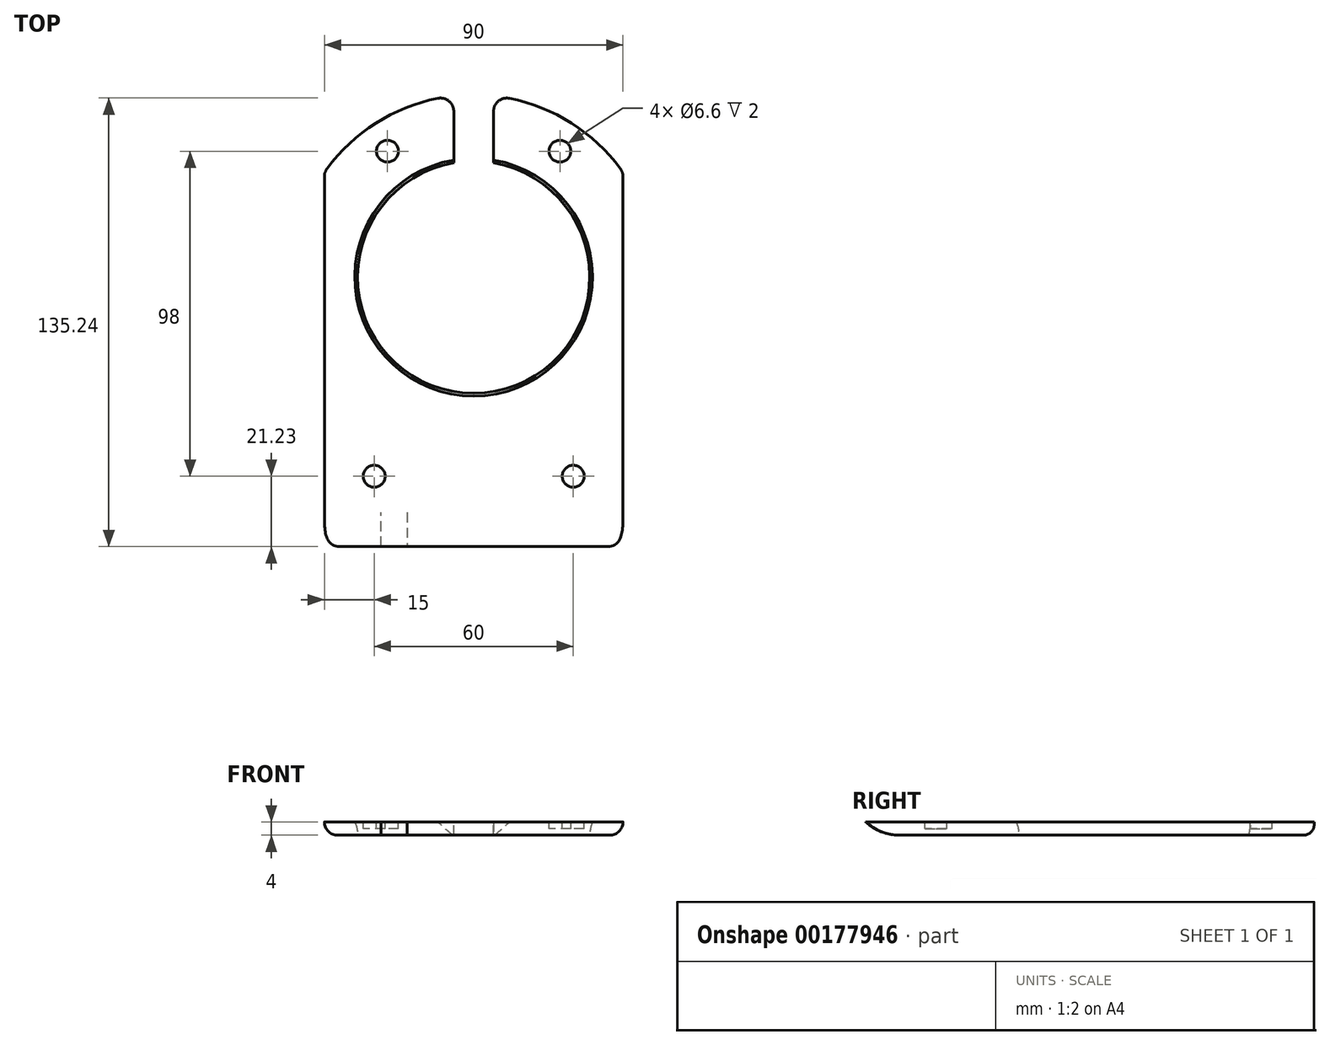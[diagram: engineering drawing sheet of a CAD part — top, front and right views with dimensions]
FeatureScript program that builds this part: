
annotation { "Feature Type Name" : "Feature", "Feature Type Description" : "" }
export const myFeature = defineFeature(function(context is Context, id is Id, definition is map)
    precondition{}
    {
        {
            var Q0;
            Q0=qCreatedBy(makeId("Top.planeOp"),FACE);
            var sketch = newSketch(context, id + "F0", { "sketchPlane" : qUnion([Q0])});
            skCircle(sketch, "E0", {"center": v(0, 0) * mm, "radius": 35 * mm});
            skLineSegment(sketch, "E1.bottom", {"start": v(45, -80) * mm, "end": v(-45, -80) * mm});
            skLineSegment(sketch, "E1.top", {"start": v(45, 80) * mm, "end": v(-45, 80) * mm});
            skLineSegment(sketch, "E1.left", {"start": v(45, -80) * mm, "end": v(45, 80) * mm});
            skLineSegment(sketch, "E1.right", {"start": v(-45, -80) * mm, "end": v(-45, 80) * mm});
            skSolve(sketch);
        }
        {
            var Q0;
            Q0=qSketchRegion(id+"F0",true);
            extrude(context, id + "F1", {"entities" : qUnion([Q0]), "depth" : 10 * mm});
        }
        {
            var Q0;
            Q0=makeQuery(id+"F1.opExtrude","CAP_EDGE",EDGE,{"disambiguationData":[OSD([sQuery(id+"F0.wireOp",EDGE,"E0")])],"isStart":false});
            fillet(context, id + "F2", {"entities" : qUnion([Q0]), "radius" : 10 * mm, "tangentPropagation" : true, "allowEdgeOverflow" : false});
        }
        {
            var Q0;
            Q0=makeQuery(id+"F2.opFillet","SPLIT",FACE,{"disambiguationData":[OD(1.0)],"derivedFrom":makeQuery(id+"F1.opExtrude","CAP_FACE",FACE,{"disambiguationData":[OSD([sQuery(id+"F0.wireOp",EDGE,"E0"),sQuery(id+"F0.wireOp",EDGE,"E1.bottom"),sQuery(id+"F0.wireOp",EDGE,"E1.top"),sQuery(id+"F0.wireOp",EDGE,"E1.left"),sQuery(id+"F0.wireOp",EDGE,"E1.right")])],"isStart":false})});
            var sketch = newSketch(context, id + "F3", { "sketchPlane" : qUnion([Q0])});
            skCircle(sketch, "E2", {"center": v(0, 0) * mm, "radius": 49 * mm});
            skLineSegment(sketch, "E3.bottom", {"start": v(45, -80) * mm, "end": v(-45, -80) * mm});
            skLineSegment(sketch, "E3.top", {"start": v(45, 80) * mm, "end": v(-45, 80) * mm});
            skLineSegment(sketch, "E3.left", {"start": v(45, -80) * mm, "end": v(45, 80) * mm});
            skLineSegment(sketch, "E3.right", {"start": v(-45, -80) * mm, "end": v(-45, 80) * mm});
            skSolve(sketch);
        }
        {
            var Q0;
            {var subQ5=sQuery(id+"F3.wireOp",EDGE,"E3.top");Q0=makeQuery(id+"F3.imprint","IMPRINT",FACE,{"disambiguationData":[TD([[makeQuery(id+"F3.imprint","IMPRINT",EDGE,{"derivedFrom":subQ5}),1.0]])]});}
            var Q1;
            {var subQ5=sQuery(id+"F3.wireOp",EDGE,"E3.bottom");Q1=makeQuery(id+"F3.imprint","IMPRINT",FACE,{"disambiguationData":[TD([[makeQuery(id+"F3.imprint","IMPRINT",EDGE,{"derivedFrom":subQ5}),-1.0]])]});}
            extrude(context, id + "F4", {"entities" : qUnion([Q0, Q1]), "operationType" : NewBodyOperationType.ADD, "depth" : 6 * mm});
        }
        {
            var Q0;
            {var subQ0=sQuery(id+"F3.wireOp",EDGE,"E2");Q0=makeQuery(id+"F4.opExtrude","CAP_EDGE",EDGE,{"disambiguationData":[OSD([subQ0]),TDD([makeQuery(id+"F3.imprint","IMPRINT",EDGE,{"disambiguationData":[TD([[makeQuery(id+"F3.imprint","INTERSECT",VERTEX,{"disambiguationData":[OD(0.0)],"derivedFrom":[subQ0,sQuery(id+"F3.wireOp",EDGE,"E3.right")]}),1.0]])],"derivedFrom":subQ0})])],"isStart":true});}
            var Q1;
            {var subQ0=sQuery(id+"F3.wireOp",EDGE,"E2");Q1=makeQuery(id+"F4.opExtrude","CAP_EDGE",EDGE,{"disambiguationData":[OSD([subQ0]),TDD([makeQuery(id+"F3.imprint","IMPRINT",EDGE,{"disambiguationData":[TD([[makeQuery(id+"F3.imprint","INTERSECT",VERTEX,{"disambiguationData":[OD(0.0)],"derivedFrom":[subQ0,sQuery(id+"F3.wireOp",EDGE,"E3.right")]}),1.0]])],"derivedFrom":subQ0})])],"isStart":false});}
            var Q2;
            {var subQ0=sQuery(id+"F3.wireOp",EDGE,"E2");Q2=makeQuery(id+"F4.opExtrude","CAP_EDGE",EDGE,{"disambiguationData":[OSD([subQ0]),TDD([makeQuery(id+"F3.imprint","IMPRINT",EDGE,{"disambiguationData":[TD([[makeQuery(id+"F3.imprint","INTERSECT",VERTEX,{"disambiguationData":[OD(1.0)],"derivedFrom":[subQ0,sQuery(id+"F3.wireOp",EDGE,"E3.right")]}),-1.0]])],"derivedFrom":subQ0})])],"isStart":true});}
            var Q3;
            {var subQ0=sQuery(id+"F3.wireOp",EDGE,"E2");Q3=makeQuery(id+"F4.opExtrude","CAP_EDGE",EDGE,{"disambiguationData":[OSD([subQ0]),TDD([makeQuery(id+"F3.imprint","IMPRINT",EDGE,{"disambiguationData":[TD([[makeQuery(id+"F3.imprint","INTERSECT",VERTEX,{"disambiguationData":[OD(1.0)],"derivedFrom":[subQ0,sQuery(id+"F3.wireOp",EDGE,"E3.right")]}),-1.0]])],"derivedFrom":subQ0})])],"isStart":false});}
            fillet(context, id + "F5", {"entities" : qUnion([Q0, Q1, Q2, Q3]), "radius" : 2 * mm, "tangentPropagation" : true, "allowEdgeOverflow" : false});
        }
        {
            var Q0;
            Q0=makeQuery(id+"F4.opExtrude","CAP_FACE",FACE,{"disambiguationData":[OSD([sQuery(id+"F3.wireOp",EDGE,"E2"),sQuery(id+"F3.wireOp",EDGE,"E3.top"),sQuery(id+"F3.wireOp",EDGE,"E3.left"),sQuery(id+"F3.wireOp",EDGE,"E3.right")])],"isStart":false});
            var sketch = newSketch(context, id + "F6", { "sketchPlane" : qUnion([Q0])});
            skCircle(sketch, "E4", {"center": v(0, 0) * mm, "radius": 55 * mm});
            skLineSegment(sketch, "E5", {"start": v(-45, 31.62) * mm, "end": v(-45, 80) * mm});
            skLineSegment(sketch, "E6", {"start": v(-45, 80) * mm, "end": v(45, 80) * mm});
            skLineSegment(sketch, "E7", {"start": v(45, 80) * mm, "end": v(45, 31.62) * mm});
            skSolve(sketch);
        }
        {
            var Q0;
            {var subQ0=sQuery(id+"F6.wireOp",EDGE,"E5");Q0=makeQuery(id+"F6.imprint","IMPRINT",FACE,{"disambiguationData":[TD([[makeQuery(id+"F6.imprint","IMPRINT",EDGE,{"derivedFrom":subQ0}),-1.0]])]});}
            extrude(context, id + "F7", {"entities" : qUnion([Q0]), "operationType" : NewBodyOperationType.REMOVE, "endBound" : BoundingType.UP_TO_NEXT, "oppositeDirection" : true, "depth" : 25 * mm});
        }
        {
            var Q0;
            Q0=makeQuery(id+"F4.opExtrude","CAP_FACE",FACE,{"disambiguationData":[OSD([sQuery(id+"F3.wireOp",EDGE,"E2"),sQuery(id+"F3.wireOp",EDGE,"E3.bottom"),sQuery(id+"F3.wireOp",EDGE,"E3.left"),sQuery(id+"F3.wireOp",EDGE,"E3.right")])],"isStart":false});
            var sketch = newSketch(context, id + "F8", { "sketchPlane" : qUnion([Q0])});
            skLineSegment(sketch, "E8.bottom", {"start": v(39, -80) * mm, "end": v(-39, -80) * mm});
            skLineSegment(sketch, "E8.top", {"start": v(39, 80) * mm, "end": v(-39, 80) * mm});
            skLineSegment(sketch, "E8.left", {"start": v(39, -80) * mm, "end": v(39, 80) * mm});
            skLineSegment(sketch, "E8.right", {"start": v(-39, -80) * mm, "end": v(-39, 80) * mm});
            skPoint(sketch, "E8.middle", {"position": v(0, 0) * mm});
            skLineSegment(sketch, "E9.bottom", {"start": v(45, -86) * mm, "end": v(-45, -86) * mm});
            skLineSegment(sketch, "E9.top", {"start": v(45, 86) * mm, "end": v(-45, 86) * mm});
            skLineSegment(sketch, "E9.left", {"start": v(45, -86) * mm, "end": v(45, 86) * mm});
            skLineSegment(sketch, "E9.right", {"start": v(-45, -86) * mm, "end": v(-45, 86) * mm});
            skArc(sketch, "E10", {"start": v(-45, -24) * mm, "mid": v(0, -51) * mm, "end": v(45, -24) * mm});
            skSolve(sketch);
        }
        {
            var Q0;
            {var subQ1=makeQuery(id+"F4.opExtrude","CAP_EDGE",EDGE,{"disambiguationData":[OSD([sQuery(id+"F3.wireOp",EDGE,"E3.bottom")])],"isStart":false});var subQ5=sQuery(id+"F8.wireOp",EDGE,"E9.left");var subQ7=makeQuery(id+"F8.imprint","INTERSECT",VERTEX,{"derivedFrom":[subQ1,subQ5]});Q0=makeQuery(id+"F8.imprint","IMPRINT",FACE,{"disambiguationData":[TD([[makeQuery(id+"F8.imprint","IMPRINT",EDGE,{"disambiguationData":[TD([[subQ7,-1.0]])],"derivedFrom":subQ5}),1.0]])]});}
            var Q1;
            {var subQ1=makeQuery(id+"F4.opExtrude","CAP_EDGE",EDGE,{"disambiguationData":[OSD([sQuery(id+"F3.wireOp",EDGE,"E3.bottom")])],"isStart":false});var subQ5=sQuery(id+"F8.wireOp",EDGE,"E9.right");var subQ6=makeQuery(id+"F8.imprint","INTERSECT",VERTEX,{"derivedFrom":[subQ1,subQ5]});Q1=makeQuery(id+"F8.imprint","IMPRINT",FACE,{"disambiguationData":[TD([[makeQuery(id+"F8.imprint","IMPRINT",EDGE,{"disambiguationData":[TD([[subQ6,-1.0]])],"derivedFrom":subQ5}),-1.0]])]});}
            extrude(context, id + "F9", {"entities" : qUnion([Q0, Q1]), "operationType" : NewBodyOperationType.ADD, "depth" : 7 * mm});
        }
        {
            var Q0;
            Q0=qCreatedBy(makeId("Right.planeOp"),FACE);
            var sketch = newSketch(context, id + "F10", { "sketchPlane" : qUnion([Q0])});
            skLineSegment(sketch, "E11", {"start": v(-64.77, -48.06) * mm, "end": v(-70.53, -49.87) * mm});
            skLineSegment(sketch, "E12", {"start": v(-85.96, 0) * mm, "end": v(-85.96, 23) * mm});
            skLineSegment(sketch, "E13", {"start": v(-79.96, 0) * mm, "end": v(-79.96, 20.33) * mm});
            skLineSegment(sketch, "E14", {"start": v(-79.96, 0) * mm, "end": v(-85.96, 0) * mm});
            skLineSegment(sketch, "E15", {"start": v(-85.96, 23) * mm, "end": v(-77.63, 23) * mm});
            skLineSegment(sketch, "E16", {"start": v(-77.63, 23) * mm, "end": v(-79.96, 20.33) * mm});
            skSolve(sketch);
        }
        {
            var Q0;
            Q0=qSketchRegion(id+"F10",true);
            extrude(context, id + "F11", {"entities" : qUnion([Q0]), "operationType" : NewBodyOperationType.ADD, "depth" : 45 * mm, "hasSecondDirection" : true, "secondDirectionOppositeDirection" : true, "secondDirectionDepth" : 45 * mm});
        }
        {
            var Q0;
            Q0=makeQuery(id+"F11.opExtrude","SWEPT_FACE",FACE,{"disambiguationData":[OSD([sQuery(id+"F10.wireOp",EDGE,"E12")])]});
            var sketch = newSketch(context, id + "F12", { "sketchPlane" : qUnion([Q0])});
            skCircle(sketch, "E17", {"center": v(-24, 19.53) * mm, "radius": 4 * mm});
            skSolve(sketch);
        }
        {
            var Q0;
            Q0=qSketchRegion(id+"F12",true);
            extrude(context, id + "F13", {"entities" : qUnion([Q0]), "operationType" : NewBodyOperationType.REMOVE, "oppositeDirection" : true, "depth" : 8.5 * mm});
        }
        {
            var Q0;
            Q0=qCreatedBy(makeId("Front.planeOp"),FACE);
            var sketch = newSketch(context, id + "F14", { "sketchPlane" : qUnion([Q0])});
            skLineSegment(sketch, "E18.bottom", {"start": v(-6, 0) * mm, "end": v(6, 0) * mm});
            skLineSegment(sketch, "E18.top", {"start": v(-6, 12) * mm, "end": v(6, 12) * mm});
            skLineSegment(sketch, "E18.left", {"start": v(-6, 0) * mm, "end": v(-6, 12) * mm});
            skLineSegment(sketch, "E18.right", {"start": v(6, 0) * mm, "end": v(6, 12) * mm});
            skPoint(sketch, "E18.middle", {"position": v(0, 6) * mm});
            skSolve(sketch);
        }
        {
            var Q0;
            Q0=qSketchRegion(id+"F14",true);
            extrude(context, id + "F15", {"entities" : qUnion([Q0]), "operationType" : NewBodyOperationType.REMOVE, "endBound" : BoundingType.THROUGH_ALL, "oppositeDirection" : true, "depth" : 25 * mm});
        }
        {
            var Q0;
            Q0=makeQuery(id+"F7.boolean.opBoolean","COPY",FACE,{"derivedFrom":makeQuery(id+"F7.opExtrude","SWEPT_FACE",FACE,{"disambiguationData":[OSD([sQuery(id+"F6.wireOp",EDGE,"E4")])]})});
            var Q1;
            Q1=makeQuery(id+"F15.boolean.opBoolean","COPY",EDGE,{"derivedFrom":makeQuery(id+"F15.opExtrude","SWEPT_EDGE",EDGE,{"disambiguationData":[OSD([sQuery(id+"F14.wireOp",EDGE,"E18.bottom"),sQuery(id+"F14.wireOp",EDGE,"E18.left")])]})});
            var Q2;
            Q2=makeQuery(id+"F15.boolean.opBoolean","COPY",EDGE,{"derivedFrom":makeQuery(id+"F15.opExtrude","SWEPT_EDGE",EDGE,{"disambiguationData":[OSD([sQuery(id+"F14.wireOp",EDGE,"E18.bottom"),sQuery(id+"F14.wireOp",EDGE,"E18.right")])]})});
            var Q3;
            Q3=makeQuery(id+"F11.boolean.opBoolean","MERGE",EDGE,{"derivedFrom":[makeQuery(id+"F1.opExtrude","CAP_EDGE",EDGE,{"disambiguationData":[OSD([sQuery(id+"F0.wireOp",EDGE,"E1.left")])],"isStart":true}),makeQuery(id+"F11.opExtrude","CAP_EDGE",EDGE,{"disambiguationData":[OSD([sQuery(id+"F10.wireOp",EDGE,"E14")])],"isStart":false})]});
            var Q4;
            Q4=makeQuery(id+"F11.boolean.opBoolean","MERGE",EDGE,{"derivedFrom":[makeQuery(id+"F1.opExtrude","CAP_EDGE",EDGE,{"disambiguationData":[OSD([sQuery(id+"F0.wireOp",EDGE,"E1.right")])],"isStart":true}),makeQuery(id+"F11.opExtrude","CAP_EDGE",EDGE,{"disambiguationData":[OSD([sQuery(id+"F10.wireOp",EDGE,"E14")])],"isStart":true})]});
            var Q5;
            Q5=makeQuery(id+"F11.opExtrude","CAP_EDGE",EDGE,{"disambiguationData":[OSD([sQuery(id+"F10.wireOp",EDGE,"E12")])],"isStart":false});
            var Q6;
            Q6=makeQuery(id+"F11.opExtrude","CAP_EDGE",EDGE,{"disambiguationData":[OSD([sQuery(id+"F10.wireOp",EDGE,"E12")])],"isStart":true});
            var Q7;
            Q7=makeQuery(id+"F11.boolean.opBoolean","MERGE",EDGE,{"derivedFrom":[makeQuery(id+"F9.opExtrude","CAP_EDGE",EDGE,{"disambiguationData":[OSD([sQuery(id+"F8.wireOp",EDGE,"E9.right")])],"isStart":false}),makeQuery(id+"F11.opExtrude","CAP_EDGE",EDGE,{"disambiguationData":[OSD([sQuery(id+"F10.wireOp",EDGE,"E15")])],"isStart":true})]});
            var Q8;
            Q8=makeQuery(id+"F11.boolean.opBoolean","MERGE",EDGE,{"derivedFrom":[makeQuery(id+"F9.opExtrude","CAP_EDGE",EDGE,{"disambiguationData":[OSD([sQuery(id+"F8.wireOp",EDGE,"E9.left")])],"isStart":false}),makeQuery(id+"F11.opExtrude","CAP_EDGE",EDGE,{"disambiguationData":[OSD([sQuery(id+"F10.wireOp",EDGE,"E15")])],"isStart":false})]});
            var Q9;
            {var subQ5=sQuery(id+"F10.wireOp",EDGE,"E12");var subQ6=sQuery(id+"F10.wireOp",EDGE,"E15");Q9=makeQuery(id+"F13.boolean.opBoolean","SPLIT",EDGE,{"disambiguationData":[TD([makeQuery(id+"F1.opExtrude","SWEPT_FACE",FACE,{"disambiguationData":[OSD([sQuery(id+"F0.wireOp",EDGE,"E1.left")])]})])],"derivedFrom":makeQuery(id+"F11.opExtrude","SWEPT_EDGE",EDGE,{"disambiguationData":[OSD([subQ5,subQ6])]})});}
            var Q10;
            {var subQ5=sQuery(id+"F10.wireOp",EDGE,"E15");var subQ6=sQuery(id+"F10.wireOp",EDGE,"E12");Q10=makeQuery(id+"F13.boolean.opBoolean","SPLIT",EDGE,{"disambiguationData":[TD([makeQuery(id+"F1.opExtrude","SWEPT_FACE",FACE,{"disambiguationData":[OSD([sQuery(id+"F0.wireOp",EDGE,"E1.right")])]})])],"derivedFrom":makeQuery(id+"F11.opExtrude","SWEPT_EDGE",EDGE,{"disambiguationData":[OSD([subQ6,subQ5])]})});}
            var Q11;
            Q11=makeQuery(id+"F13.boolean.opBoolean","COPY",EDGE,{"derivedFrom":makeQuery(id+"F13.opExtrude","CAP_EDGE",EDGE,{"disambiguationData":[OSD([sQuery(id+"F12.wireOp",EDGE,"E17")])],"isStart":true})});
            fillet(context, id + "F16", {"entities" : qUnion([Q0, Q1, Q2, Q3, Q4, Q5, Q6, Q7, Q8, Q9, Q10, Q11]), "radius" : 4 * mm, "tangentPropagation" : true, "allowEdgeOverflow" : false});
        }
        {
            var Q0;
            {var subQ0=sQuery(id+"F8.wireOp",EDGE,"E10");var subQ1=sQuery(id+"F3.wireOp",EDGE,"E3.bottom");Q0=makeQuery(id+"F13.boolean.opBoolean","INTERSECT",EDGE,{"disambiguationData":[OD(1.0)],"derivedFrom":[makeQuery(id+"F11.boolean.opBoolean","MERGE",FACE,{"derivedFrom":[makeQuery(id+"F9.opExtrude","CAP_FACE",FACE,{"disambiguationData":[OSD([subQ1,sQuery(id+"F8.wireOp",EDGE,"E8.left"),sQuery(id+"F8.wireOp",EDGE,"E9.left"),subQ0])],"isStart":false}),makeQuery(id+"F9.opExtrude","CAP_FACE",FACE,{"disambiguationData":[OSD([subQ1,sQuery(id+"F8.wireOp",EDGE,"E8.right"),sQuery(id+"F8.wireOp",EDGE,"E9.right"),subQ0])],"isStart":false}),makeQuery(id+"F11.opExtrude","SWEPT_FACE",FACE,{"disambiguationData":[OSD([sQuery(id+"F10.wireOp",EDGE,"E15")])]})]}),makeQuery(id+"F13.opExtrude","SWEPT_FACE",FACE,{"disambiguationData":[OSD([sQuery(id+"F12.wireOp",EDGE,"E17")])]})]});}
            var Q1;
            {var subQ0=sQuery(id+"F8.wireOp",EDGE,"E10");var subQ1=sQuery(id+"F3.wireOp",EDGE,"E3.bottom");Q1=makeQuery(id+"F13.boolean.opBoolean","INTERSECT",EDGE,{"disambiguationData":[OD(0.0)],"derivedFrom":[makeQuery(id+"F11.boolean.opBoolean","MERGE",FACE,{"derivedFrom":[makeQuery(id+"F9.opExtrude","CAP_FACE",FACE,{"disambiguationData":[OSD([subQ1,sQuery(id+"F8.wireOp",EDGE,"E8.left"),sQuery(id+"F8.wireOp",EDGE,"E9.left"),subQ0])],"isStart":false}),makeQuery(id+"F9.opExtrude","CAP_FACE",FACE,{"disambiguationData":[OSD([subQ1,sQuery(id+"F8.wireOp",EDGE,"E8.right"),sQuery(id+"F8.wireOp",EDGE,"E9.right"),subQ0])],"isStart":false}),makeQuery(id+"F11.opExtrude","SWEPT_FACE",FACE,{"disambiguationData":[OSD([sQuery(id+"F10.wireOp",EDGE,"E15")])]})]}),makeQuery(id+"F13.opExtrude","SWEPT_FACE",FACE,{"disambiguationData":[OSD([sQuery(id+"F12.wireOp",EDGE,"E17")])]})]});}
            var Q2;
            Q2=makeQuery(id+"F13.boolean.opBoolean","COPY",EDGE,{"derivedFrom":makeQuery(id+"F13.opExtrude","CAP_EDGE",EDGE,{"disambiguationData":[OSD([sQuery(id+"F12.wireOp",EDGE,"E17")])],"isStart":false})});
            var Q3;
            Q3=makeQuery(id+"F9.opExtrude","CAP_EDGE",EDGE,{"disambiguationData":[OSD([sQuery(id+"F8.wireOp",EDGE,"E8.left")])],"isStart":true});
            var Q4;
            Q4=makeQuery(id+"F9.opExtrude","CAP_EDGE",EDGE,{"disambiguationData":[OSD([sQuery(id+"F8.wireOp",EDGE,"E8.right")])],"isStart":true});
            var Q5;
            Q5=makeQuery(id+"F9.opExtrude","CAP_EDGE",EDGE,{"disambiguationData":[OSD([sQuery(id+"F8.wireOp",EDGE,"E8.right")])],"isStart":false});
            var Q6;
            Q6=makeQuery(id+"F9.opExtrude","CAP_EDGE",EDGE,{"disambiguationData":[OSD([sQuery(id+"F8.wireOp",EDGE,"E8.left")])],"isStart":false});
            var Q7;
            {var subQ0=sQuery(id+"F3.wireOp",EDGE,"E3.left");var subQ1=sQuery(id+"F3.wireOp",EDGE,"E2");Q7=makeQuery(id+"F5.opFillet","BLEND_EDGE",EDGE,{"blendedFrom":[makeQuery(id+"F4.opExtrude","CAP_EDGE",EDGE,{"disambiguationData":[OSD([subQ1]),TDD([makeQuery(id+"F3.imprint","IMPRINT",EDGE,{"disambiguationData":[TD([[makeQuery(id+"F3.imprint","INTERSECT",VERTEX,{"disambiguationData":[OD(1.0)],"derivedFrom":[subQ1,sQuery(id+"F3.wireOp",EDGE,"E3.right")]}),-1.0]])],"derivedFrom":subQ1})])],"isStart":false}),makeQuery(id+"F4.boolean.opBoolean","MERGE",FACE,{"derivedFrom":[makeQuery(id+"F1.opExtrude","SWEPT_FACE",FACE,{"disambiguationData":[OSD([sQuery(id+"F0.wireOp",EDGE,"E1.left")])]}),makeQuery(id+"F4.opExtrude","SWEPT_FACE",FACE,{"disambiguationData":[OSD([subQ0]),TDD([makeQuery(id+"F3.imprint","IMPRINT",EDGE,{"disambiguationData":[TD([[makeQuery(id+"F3.imprint","INTERSECT",VERTEX,{"derivedFrom":[sQuery(id+"F3.wireOp",EDGE,"E3.bottom"),subQ0]}),-1.0]])],"derivedFrom":subQ0})])]}),makeQuery(id+"F4.opExtrude","SWEPT_FACE",FACE,{"disambiguationData":[OSD([subQ0]),TDD([makeQuery(id+"F3.imprint","IMPRINT",EDGE,{"disambiguationData":[TD([[makeQuery(id+"F3.imprint","INTERSECT",VERTEX,{"derivedFrom":[sQuery(id+"F3.wireOp",EDGE,"E3.top"),subQ0]}),1.0]])],"derivedFrom":subQ0})])]})]})],"blendedInto":[makeQuery(id+"F4.boolean.opBoolean","MERGE",FACE,{"derivedFrom":[makeQuery(id+"F1.opExtrude","SWEPT_FACE",FACE,{"disambiguationData":[OSD([sQuery(id+"F0.wireOp",EDGE,"E1.left")])]}),makeQuery(id+"F4.opExtrude","SWEPT_FACE",FACE,{"disambiguationData":[OSD([subQ0]),TDD([makeQuery(id+"F3.imprint","IMPRINT",EDGE,{"disambiguationData":[TD([[makeQuery(id+"F3.imprint","INTERSECT",VERTEX,{"derivedFrom":[sQuery(id+"F3.wireOp",EDGE,"E3.bottom"),subQ0]}),-1.0]])],"derivedFrom":subQ0})])]}),makeQuery(id+"F4.opExtrude","SWEPT_FACE",FACE,{"disambiguationData":[OSD([subQ0]),TDD([makeQuery(id+"F3.imprint","IMPRINT",EDGE,{"disambiguationData":[TD([[makeQuery(id+"F3.imprint","INTERSECT",VERTEX,{"derivedFrom":[sQuery(id+"F3.wireOp",EDGE,"E3.top"),subQ0]}),1.0]])],"derivedFrom":subQ0})])]})]})]});}
            var Q8;
            {var subQ0=sQuery(id+"F3.wireOp",EDGE,"E3.right");var subQ1=sQuery(id+"F3.wireOp",EDGE,"E2");var subQ2=makeQuery(id+"F3.imprint","INTERSECT",VERTEX,{"disambiguationData":[OD(1.0)],"derivedFrom":[subQ1,subQ0]});Q8=makeQuery(id+"F5.opFillet","BLEND_EDGE",EDGE,{"blendedFrom":[makeQuery(id+"F4.opExtrude","CAP_EDGE",EDGE,{"disambiguationData":[OSD([subQ1]),TDD([makeQuery(id+"F3.imprint","IMPRINT",EDGE,{"disambiguationData":[TD([[subQ2,-1.0]])],"derivedFrom":subQ1})])],"isStart":false}),makeQuery(id+"F4.boolean.opBoolean","MERGE",FACE,{"derivedFrom":[makeQuery(id+"F1.opExtrude","SWEPT_FACE",FACE,{"disambiguationData":[OSD([sQuery(id+"F0.wireOp",EDGE,"E1.right")])]}),makeQuery(id+"F4.opExtrude","SWEPT_FACE",FACE,{"disambiguationData":[OSD([subQ0]),TDD([makeQuery(id+"F3.imprint","IMPRINT",EDGE,{"disambiguationData":[TD([[makeQuery(id+"F3.imprint","INTERSECT",VERTEX,{"derivedFrom":[sQuery(id+"F3.wireOp",EDGE,"E3.bottom"),subQ0]}),-1.0]])],"derivedFrom":subQ0})])]}),makeQuery(id+"F4.opExtrude","SWEPT_FACE",FACE,{"disambiguationData":[OSD([subQ0]),TDD([makeQuery(id+"F3.imprint","IMPRINT",EDGE,{"disambiguationData":[TD([[makeQuery(id+"F3.imprint","INTERSECT",VERTEX,{"derivedFrom":[sQuery(id+"F3.wireOp",EDGE,"E3.top"),subQ0]}),1.0]])],"derivedFrom":subQ0})])]})]})],"blendedInto":[makeQuery(id+"F4.boolean.opBoolean","MERGE",FACE,{"derivedFrom":[makeQuery(id+"F1.opExtrude","SWEPT_FACE",FACE,{"disambiguationData":[OSD([sQuery(id+"F0.wireOp",EDGE,"E1.right")])]}),makeQuery(id+"F4.opExtrude","SWEPT_FACE",FACE,{"disambiguationData":[OSD([subQ0]),TDD([makeQuery(id+"F3.imprint","IMPRINT",EDGE,{"disambiguationData":[TD([[makeQuery(id+"F3.imprint","INTERSECT",VERTEX,{"derivedFrom":[sQuery(id+"F3.wireOp",EDGE,"E3.bottom"),subQ0]}),-1.0]])],"derivedFrom":subQ0})])]}),makeQuery(id+"F4.opExtrude","SWEPT_FACE",FACE,{"disambiguationData":[OSD([subQ0]),TDD([makeQuery(id+"F3.imprint","IMPRINT",EDGE,{"disambiguationData":[TD([[makeQuery(id+"F3.imprint","INTERSECT",VERTEX,{"derivedFrom":[sQuery(id+"F3.wireOp",EDGE,"E3.top"),subQ0]}),1.0]])],"derivedFrom":subQ0})])]})]})]});}
            fillet(context, id + "F17", {"entities" : qUnion([Q0, Q1, Q2, Q3, Q4, Q5, Q6, Q7, Q8]), "radius" : 2 * mm, "tangentPropagation" : true, "allowEdgeOverflow" : false});
        }
        {
            var Q0;
            {var subQ0=sQuery(id+"F8.wireOp",EDGE,"E10");var subQ1=sQuery(id+"F3.wireOp",EDGE,"E3.left");var subQ2=sQuery(id+"F3.wireOp",EDGE,"E2");Q0=makeQuery(id+"F17.opFillet","BLEND_EDGE",EDGE,{"blendedFrom":[makeQuery(id+"F4.opExtrude","SWEPT_EDGE",EDGE,{"disambiguationData":[OSD([subQ2,subQ1]),TDD([makeQuery(id+"F3.imprint","INTERSECT",VERTEX,{"disambiguationData":[OD(1.0)],"derivedFrom":[subQ2,subQ1]})])]}),makeQuery(id+"F9.opExtrude","SWEPT_FACE",FACE,{"disambiguationData":[OSD([subQ0]),TDD([makeQuery(id+"F8.imprint","IMPRINT",EDGE,{"disambiguationData":[TD([[makeQuery(id+"F8.imprint","INTERSECT",VERTEX,{"derivedFrom":[sQuery(id+"F8.wireOp",EDGE,"E9.left"),subQ0]}),-1.0]])],"derivedFrom":subQ0})])]})],"blendedInto":[makeQuery(id+"F9.opExtrude","SWEPT_FACE",FACE,{"disambiguationData":[OSD([subQ0]),TDD([makeQuery(id+"F8.imprint","IMPRINT",EDGE,{"disambiguationData":[TD([[makeQuery(id+"F8.imprint","INTERSECT",VERTEX,{"derivedFrom":[sQuery(id+"F8.wireOp",EDGE,"E9.left"),subQ0]}),-1.0]])],"derivedFrom":subQ0})])]})]});}
            var Q1;
            {var subQ0=sQuery(id+"F8.wireOp",EDGE,"E10");var subQ1=sQuery(id+"F3.wireOp",EDGE,"E3.right");var subQ2=sQuery(id+"F3.wireOp",EDGE,"E2");Q1=makeQuery(id+"F17.opFillet","BLEND_EDGE",EDGE,{"blendedFrom":[makeQuery(id+"F4.opExtrude","SWEPT_EDGE",EDGE,{"disambiguationData":[OSD([subQ2,subQ1]),TDD([makeQuery(id+"F3.imprint","INTERSECT",VERTEX,{"disambiguationData":[OD(1.0)],"derivedFrom":[subQ2,subQ1]})])]}),makeQuery(id+"F9.opExtrude","SWEPT_FACE",FACE,{"disambiguationData":[OSD([subQ0]),TDD([makeQuery(id+"F8.imprint","IMPRINT",EDGE,{"disambiguationData":[TD([[makeQuery(id+"F8.imprint","INTERSECT",VERTEX,{"derivedFrom":[sQuery(id+"F8.wireOp",EDGE,"E9.right"),subQ0]}),1.0]])],"derivedFrom":subQ0})])]})],"blendedInto":[makeQuery(id+"F9.opExtrude","SWEPT_FACE",FACE,{"disambiguationData":[OSD([subQ0]),TDD([makeQuery(id+"F8.imprint","IMPRINT",EDGE,{"disambiguationData":[TD([[makeQuery(id+"F8.imprint","INTERSECT",VERTEX,{"derivedFrom":[sQuery(id+"F8.wireOp",EDGE,"E9.right"),subQ0]}),1.0]])],"derivedFrom":subQ0})])]})]});}
            var Q2;
            {var subQ0=sQuery(id+"F3.wireOp",EDGE,"E3.right");var subQ1=sQuery(id+"F3.wireOp",EDGE,"E2");var subQ2=makeQuery(id+"F3.imprint","INTERSECT",VERTEX,{"disambiguationData":[OD(1.0)],"derivedFrom":[subQ1,subQ0]});Q2=makeQuery(id+"F17.opFillet","BLEND_EDGE",EDGE,{"blendedFrom":[makeQuery(id+"F4.opExtrude","SWEPT_EDGE",EDGE,{"disambiguationData":[OSD([subQ1,subQ0]),TDD([subQ2])]}),makeQuery(id+"F5.opFillet","BLEND_FACE",FACE,{"disambiguationData":[OSD([subQ1]),TDD([makeQuery(id+"F4.opExtrude","CAP_EDGE",EDGE,{"disambiguationData":[OSD([subQ1]),TDD([makeQuery(id+"F3.imprint","IMPRINT",EDGE,{"disambiguationData":[TD([[subQ2,-1.0]])],"derivedFrom":subQ1})])],"isStart":false})])]})],"blendedInto":[makeQuery(id+"F5.opFillet","BLEND_FACE",FACE,{"disambiguationData":[OSD([subQ1]),TDD([makeQuery(id+"F4.opExtrude","CAP_EDGE",EDGE,{"disambiguationData":[OSD([subQ1]),TDD([makeQuery(id+"F3.imprint","IMPRINT",EDGE,{"disambiguationData":[TD([[subQ2,-1.0]])],"derivedFrom":subQ1})])],"isStart":false})])]})]});}
            var Q3;
            {var subQ0=sQuery(id+"F3.wireOp",EDGE,"E2");var subQ1=sQuery(id+"F3.wireOp",EDGE,"E3.left");var subQ2=makeQuery(id+"F3.imprint","INTERSECT",VERTEX,{"disambiguationData":[OD(1.0)],"derivedFrom":[subQ0,subQ1]});Q3=makeQuery(id+"F17.opFillet","BLEND_EDGE",EDGE,{"blendedFrom":[makeQuery(id+"F4.opExtrude","SWEPT_EDGE",EDGE,{"disambiguationData":[OSD([subQ0,subQ1]),TDD([subQ2])]}),makeQuery(id+"F5.opFillet","BLEND_FACE",FACE,{"disambiguationData":[OSD([subQ0]),TDD([makeQuery(id+"F4.opExtrude","CAP_EDGE",EDGE,{"disambiguationData":[OSD([subQ0]),TDD([makeQuery(id+"F3.imprint","IMPRINT",EDGE,{"disambiguationData":[TD([[makeQuery(id+"F3.imprint","INTERSECT",VERTEX,{"disambiguationData":[OD(1.0)],"derivedFrom":[subQ0,sQuery(id+"F3.wireOp",EDGE,"E3.right")]}),-1.0]])],"derivedFrom":subQ0})])],"isStart":false})])]})],"blendedInto":[makeQuery(id+"F5.opFillet","BLEND_FACE",FACE,{"disambiguationData":[OSD([subQ0]),TDD([makeQuery(id+"F4.opExtrude","CAP_EDGE",EDGE,{"disambiguationData":[OSD([subQ0]),TDD([makeQuery(id+"F3.imprint","IMPRINT",EDGE,{"disambiguationData":[TD([[makeQuery(id+"F3.imprint","INTERSECT",VERTEX,{"disambiguationData":[OD(1.0)],"derivedFrom":[subQ0,sQuery(id+"F3.wireOp",EDGE,"E3.right")]}),-1.0]])],"derivedFrom":subQ0})])],"isStart":false})])]})]});}
            var Q4;
            {var subQ0=sQuery(id+"F8.wireOp",EDGE,"E10");var subQ1=sQuery(id+"F8.wireOp",EDGE,"E9.right");Q4=makeQuery(id+"F16.opFillet","BLEND_EDGE",EDGE,{"blendedFrom":[makeQuery(id+"F11.boolean.opBoolean","MERGE",EDGE,{"derivedFrom":[makeQuery(id+"F9.opExtrude","CAP_EDGE",EDGE,{"disambiguationData":[OSD([subQ1])],"isStart":false}),makeQuery(id+"F11.opExtrude","CAP_EDGE",EDGE,{"disambiguationData":[OSD([sQuery(id+"F10.wireOp",EDGE,"E15")])],"isStart":true})]}),makeQuery(id+"F9.opExtrude","SWEPT_FACE",FACE,{"disambiguationData":[OSD([subQ0]),TDD([makeQuery(id+"F8.imprint","IMPRINT",EDGE,{"disambiguationData":[TD([[makeQuery(id+"F8.imprint","INTERSECT",VERTEX,{"derivedFrom":[subQ1,subQ0]}),1.0]])],"derivedFrom":subQ0})])]})],"blendedInto":[makeQuery(id+"F9.opExtrude","SWEPT_FACE",FACE,{"disambiguationData":[OSD([subQ0]),TDD([makeQuery(id+"F8.imprint","IMPRINT",EDGE,{"disambiguationData":[TD([[makeQuery(id+"F8.imprint","INTERSECT",VERTEX,{"derivedFrom":[subQ1,subQ0]}),1.0]])],"derivedFrom":subQ0})])]})]});}
            var Q5;
            {var subQ0=sQuery(id+"F8.wireOp",EDGE,"E10");var subQ1=sQuery(id+"F8.wireOp",EDGE,"E9.left");Q5=makeQuery(id+"F16.opFillet","BLEND_EDGE",EDGE,{"blendedFrom":[makeQuery(id+"F11.boolean.opBoolean","MERGE",EDGE,{"derivedFrom":[makeQuery(id+"F9.opExtrude","CAP_EDGE",EDGE,{"disambiguationData":[OSD([subQ1])],"isStart":false}),makeQuery(id+"F11.opExtrude","CAP_EDGE",EDGE,{"disambiguationData":[OSD([sQuery(id+"F10.wireOp",EDGE,"E15")])],"isStart":false})]}),makeQuery(id+"F9.opExtrude","SWEPT_FACE",FACE,{"disambiguationData":[OSD([subQ0]),TDD([makeQuery(id+"F8.imprint","IMPRINT",EDGE,{"disambiguationData":[TD([[makeQuery(id+"F8.imprint","INTERSECT",VERTEX,{"derivedFrom":[subQ1,subQ0]}),-1.0]])],"derivedFrom":subQ0})])]})],"blendedInto":[makeQuery(id+"F9.opExtrude","SWEPT_FACE",FACE,{"disambiguationData":[OSD([subQ0]),TDD([makeQuery(id+"F8.imprint","IMPRINT",EDGE,{"disambiguationData":[TD([[makeQuery(id+"F8.imprint","INTERSECT",VERTEX,{"derivedFrom":[subQ1,subQ0]}),-1.0]])],"derivedFrom":subQ0})])]})]});}
            var Q6;
            {var subQ0=sQuery(id+"F10.wireOp",EDGE,"E15");var subQ3=sQuery(id+"F8.wireOp",EDGE,"E8.left");var subQ4=sQuery(id+"F10.wireOp",EDGE,"E16");Q6=makeQuery(id+"F13.boolean.opBoolean","SPLIT",EDGE,{"disambiguationData":[TD([makeQuery(id+"F9.opExtrude","SWEPT_FACE",FACE,{"disambiguationData":[OSD([subQ3])]})])],"derivedFrom":makeQuery(id+"F11.opExtrude","SWEPT_EDGE",EDGE,{"disambiguationData":[OSD([subQ0,subQ4])]})});}
            var Q7;
            {var subQ0=sQuery(id+"F10.wireOp",EDGE,"E15");var subQ2=sQuery(id+"F8.wireOp",EDGE,"E8.right");var subQ4=sQuery(id+"F10.wireOp",EDGE,"E16");Q7=makeQuery(id+"F13.boolean.opBoolean","SPLIT",EDGE,{"disambiguationData":[TD([makeQuery(id+"F9.opExtrude","SWEPT_FACE",FACE,{"disambiguationData":[OSD([subQ2])]})])],"derivedFrom":makeQuery(id+"F11.opExtrude","SWEPT_EDGE",EDGE,{"disambiguationData":[OSD([subQ0,subQ4])]})});}
            var Q8;
            Q8=makeQuery(id+"F15.boolean.opBoolean","COPY",EDGE,{"derivedFrom":makeQuery(id+"F15.opExtrude","SWEPT_EDGE",EDGE,{"disambiguationData":[OSD([sQuery(id+"F14.wireOp",EDGE,"E18.top"),sQuery(id+"F14.wireOp",EDGE,"E18.right")])]})});
            var Q9;
            Q9=makeQuery(id+"F15.boolean.opBoolean","COPY",EDGE,{"derivedFrom":makeQuery(id+"F15.opExtrude","SWEPT_EDGE",EDGE,{"disambiguationData":[OSD([sQuery(id+"F14.wireOp",EDGE,"E18.top"),sQuery(id+"F14.wireOp",EDGE,"E18.left")])]})});
            fillet(context, id + "F18", {"entities" : qUnion([Q0, Q1, Q2, Q3, Q4, Q5, Q6, Q7, Q8, Q9]), "radius" : 1 * mm, "tangentPropagation" : true, "allowEdgeOverflow" : false});
        }
        {
            var Q0;
            Q0=makeQuery(id+"F11.opExtrude","SWEPT_EDGE",EDGE,{"disambiguationData":[OSD([sQuery(id+"F10.wireOp",EDGE,"E12"),sQuery(id+"F10.wireOp",EDGE,"E14")])]});
            fillet(context, id + "F19", {"entities" : qUnion([Q0]), "radius" : 15 * mm, "tangentPropagation" : true, "allowEdgeOverflow" : false});
        }
        {
            var Q0;
            {var subQ0=sQuery(id+"F8.wireOp",EDGE,"E8.left");var subQ3=sQuery(id+"F8.wireOp",EDGE,"E9.left");var subQ4=sQuery(id+"F3.wireOp",EDGE,"E3.bottom");var subQ5=sQuery(id+"F8.wireOp",EDGE,"E10");var subQ8=sQuery(id+"F10.wireOp",EDGE,"E15");Q0=makeQuery(id+"F13.boolean.opBoolean","SPLIT",FACE,{"disambiguationData":[TD([makeQuery(id+"F1.opExtrude","SWEPT_FACE",FACE,{"disambiguationData":[OSD([sQuery(id+"F0.wireOp",EDGE,"E1.left")])]})])],"derivedFrom":makeQuery(id+"F11.boolean.opBoolean","MERGE",FACE,{"derivedFrom":[makeQuery(id+"F9.opExtrude","CAP_FACE",FACE,{"disambiguationData":[OSD([subQ4,subQ0,subQ3,subQ5])],"isStart":false}),makeQuery(id+"F9.opExtrude","CAP_FACE",FACE,{"disambiguationData":[OSD([subQ4,sQuery(id+"F8.wireOp",EDGE,"E8.right"),sQuery(id+"F8.wireOp",EDGE,"E9.right"),subQ5])],"isStart":false}),makeQuery(id+"F11.opExtrude","SWEPT_FACE",FACE,{"disambiguationData":[OSD([subQ8])]})]})});}
            var sketch = newSketch(context, id + "F20", { "sketchPlane" : qUnion([Q0])});
            skLineSegment(sketch, "E19.bottom", {"start": v(47.13, -87.88) * mm, "end": v(-47.13, -87.88) * mm});
            skLineSegment(sketch, "E19.top", {"start": v(47.13, 87.88) * mm, "end": v(-47.13, 87.88) * mm});
            skLineSegment(sketch, "E19.left", {"start": v(47.13, -87.88) * mm, "end": v(47.13, 87.88) * mm});
            skLineSegment(sketch, "E19.right", {"start": v(-47.13, -87.88) * mm, "end": v(-47.13, 87.88) * mm});
            skPoint(sketch, "E19.middle", {"position": v(0, 0) * mm});
            skSolve(sketch);
        }
        {
            var Q0;
            Q0 = qSketchRegion(id + "F20", true);
            extrude(context, id + "F21", {"entities" : qUnion([Q0]), "operationType" : NewBodyOperationType.REMOVE, "oppositeDirection" : true, "depth" : 19 * mm});
        }
        {
            var Q0;
            Q0=makeQuery(id+"F21.boolean.opBoolean","COPY",FACE,{"derivedFrom":makeQuery(id+"F21.opExtrude","CAP_FACE",FACE,{"disambiguationData":[OSD([sQuery(id+"F20.wireOp",EDGE,"E19.bottom"),sQuery(id+"F20.wireOp",EDGE,"E19.top"),sQuery(id+"F20.wireOp",EDGE,"E19.left"),sQuery(id+"F20.wireOp",EDGE,"E19.right")])],"isStart":false})});
            var sketch = newSketch(context, id + "F22", { "sketchPlane" : qUnion([Q0])});
            skCircle(sketch, "E20", {"center": v(-30, -60) * mm, "radius": 3.3 * mm});
            skCircle(sketch, "E21", {"center": v(-26, 38) * mm, "radius": 3.3 * mm});
            skCircle(sketch, "E22.MirrorC", {"center": v(26, 38) * mm, "radius": 3.3 * mm});
            skCircle(sketch, "E23.MirrorC", {"center": v(30, -60) * mm, "radius": 3.3 * mm});
            skSolve(sketch);
        }
        {
            var Q0;
            Q0 = qSketchRegion(id + "F22", true);
            extrude(context, id + "F23", {"entities" : qUnion([Q0]), "operationType" : NewBodyOperationType.REMOVE, "oppositeDirection" : true, "depth" : 2 * mm});
        }
    });
